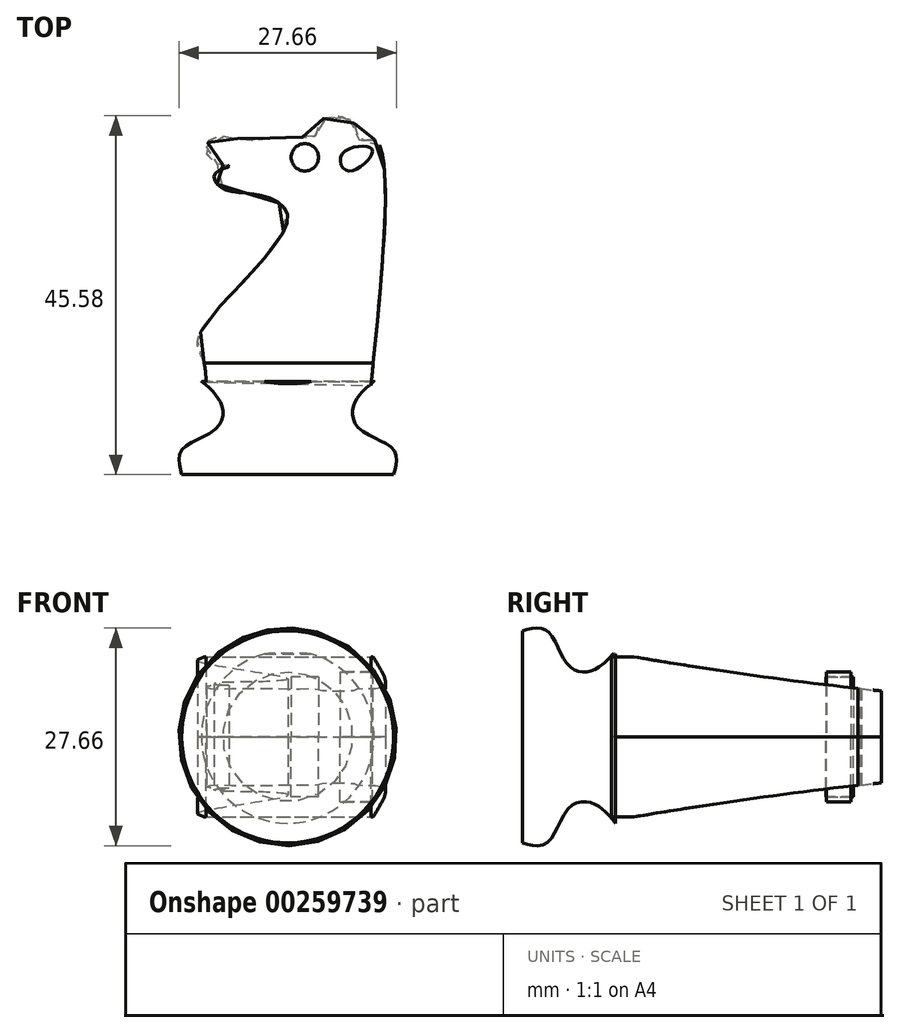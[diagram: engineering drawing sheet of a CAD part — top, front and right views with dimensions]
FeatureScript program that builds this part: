
annotation { "Feature Type Name" : "Feature", "Feature Type Description" : "" }
export const myFeature = defineFeature(function(context is Context, id is Id, definition is map)
    precondition{}
    {
        {
            var Q0;
            Q0=qCreatedBy(makeId("Top.planeOp"),FACE);
            var sketch = newSketch(context, id + "F0", { "sketchPlane" : qUnion([Q0])});
            skLineSegment(sketch, "E0", {"start": v(0, 0) * mm, "end": v(13.46, 0) * mm});
            skFitSpline(sketch, "E1", {"points": [v(13.46, 0) * mm, v(13.46, 3.13) * mm, v(9.08, 5.84) * mm, v(8.45, 8.97) * mm, v(10.97, 11.83) * mm], "startDerivative": vector(4.14, 14.83) * mm, "endDerivative": vector(11.05, 8.65) * mm});
            skLineSegment(sketch, "E2", {"start": v(0, 0) * mm, "end": v(0, 11.83) * mm});
            skLineSegment(sketch, "E3", {"start": v(0, 11.83) * mm, "end": v(10.97, 11.83) * mm});
            skSolve(sketch);
        }
        {
            var Q0;
            Q0=makeQuery(id+"F0.imprint","IMPRINT",FACE,{"disambiguationData":[TD([[makeQuery(id+"F0.imprint","IMPRINT",EDGE,{"derivedFrom":sQuery(id+"F0.wireOp",EDGE,"E0")}),1.0]])]});
            var Q1;
            Q1=sQuery(id+"F0.wireOp",EDGE,"E2");
            revolve(context, id + "F1", {"entities" : qUnion([Q0]), "axis" : qUnion([Q1]), "revolveType" : RevolveType.FULL});
        }
        {
            var Q0;
            Q0=qCreatedBy(makeId("Top.planeOp"),FACE);
            var sketch = newSketch(context, id + "F2", { "sketchPlane" : qUnion([Q0])});
            skFitSpline(sketch, "E4", {"points": [v(-10.37, 11.73) * mm, v(-10.79, 14.67) * mm, v(-11.2, 17.8) * mm, v(0, 32.26) * mm, v(-3.25, 35.4) * mm, v(-7.44, 36.04) * mm, v(-9.11, 37.08) * mm, v(-9.11, 38.34) * mm, v(-7.44, 39.18) * mm, v(-9.74, 39.8) * mm, v(-9.74, 42.74) * mm, v(-5.55, 42.53) * mm, v(0, 42.95) * mm, v(3.67, 43.16) * mm, v(4.3, 45.04) * mm, v(8.28, 44.83) * mm, v(9.11, 42.53) * mm, v(11, 42.53) * mm, v(10.58, 11.31) * mm], "startDerivative": vector(-2.35, 66.57) * mm, "endDerivative": vector(-30.17, -301.15) * mm});
            skLineSegment(sketch, "E5", {"start": v(-10.37, 11.73) * mm, "end": v(10.58, 11.31) * mm});
            skSolve(sketch);
        }
        {
            var Q0;
            Q0 = qSketchRegion(id + "F2", true);
            extrude(context, id + "F3", {"entities" : qUnion([Q0]), "depth" : 10.16 * mm});
        }
        {
            var Q0;
            Q0=makeQuery(id+"F2.imprint","IMPRINT",FACE,{"disambiguationData":[TD([[makeQuery(id+"F2.imprint","IMPRINT",EDGE,{"derivedFrom":sQuery(id+"F2.wireOp",EDGE,"E4")}),-1.0]])]});
            var sketch = newSketch(context, id + "F4", { "sketchPlane" : qUnion([Q0])});
            skCircle(sketch, "E6", {"center": v(2.17, 40.3) * mm, "radius": 1.73 * mm});
            skSolve(sketch);
        }
        {
            var Q0;
            Q0=makeQuery(id+"F2.imprint","IMPRINT",FACE,{"disambiguationData":[TD([[makeQuery(id+"F2.imprint","IMPRINT",EDGE,{"derivedFrom":sQuery(id+"F2.wireOp",EDGE,"E4")}),-1.0]])]});
            var sketch = newSketch(context, id + "F5", { "sketchPlane" : qUnion([Q0])});
            skFitSpline(sketch, "E7", {"points": [v(6.9, 40.71) * mm, v(10.46, 41.55) * mm, v(10.46, 40.3) * mm, v(7.53, 38.62) * mm, v(6.9, 40.71) * mm]});
            skSolve(sketch);
        }
        {
            var Q0;
            Q0=qCreatedBy(makeId("Right.planeOp"),FACE);
            var sketch = newSketch(context, id + "F6", { "sketchPlane" : qUnion([Q0])});
            skFitSpline(sketch, "E8", {"points": [v(76.54, 4.77) * mm, v(51.13, 5.34) * mm, v(7.54, 11.33) * mm], "startDerivative": vector(-52.97, -0.72) * mm, "endDerivative": vector(-64.6, 11.97) * mm});
            skLineSegment(sketch, "E9", {"start": v(76.54, 4.77) * mm, "end": v(76.54, 37.7) * mm});
            skLineSegment(sketch, "E10", {"start": v(76.54, 37.7) * mm, "end": v(7.54, 11.33) * mm});
            skSolve(sketch);
        }
        {
            var Q0;
            Q0=makeQuery(id+"F6.imprint","IMPRINT",FACE,{"disambiguationData":[TD([[makeQuery(id+"F6.imprint","IMPRINT",EDGE,{"derivedFrom":sQuery(id+"F6.wireOp",EDGE,"E8")}),-1.0]])]});
            extrude(context, id + "F7", {"entities" : qUnion([Q0]), "operationType" : NewBodyOperationType.REMOVE, "oppositeDirection" : true, "depth" : 25.4 * mm});
        }
        {
            var Q0;
            Q0 = qSketchRegion(id + "F6", true);
            extrude(context, id + "F8", {"entities" : qUnion([Q0]), "operationType" : NewBodyOperationType.REMOVE, "depth" : 25.4 * mm});
        }
        {
            var Q0;
            Q0 = qSketchRegion(id + "F4", true);
            extrude(context, id + "F9", {"entities" : qUnion([Q0]), "depth" : 7.62 * mm});
        }
        {
            var Q0;
            Q0 = qSketchRegion(id + "F5", true);
            extrude(context, id + "F10", {"entities" : qUnion([Q0]), "depth" : 8.25 * mm});
        }
        {
            var Q0;
            Q0=makeQuery(id+"F3.opExtrude","SWEPT_BODY",BODY,{"disambiguationData":[OSD([sQuery(id+"F2.wireOp",EDGE,"E4"),sQuery(id+"F2.wireOp",EDGE,"E5")])]});
            var Q1;
            Q1=makeQuery(id+"F10.opExtrude","SWEPT_BODY",BODY,{"disambiguationData":[OSD([sQuery(id+"F5.wireOp",EDGE,"E7")])]});
            var Q2;
            Q2=makeQuery(id+"F9.opExtrude","SWEPT_BODY",BODY,{"disambiguationData":[OSD([sQuery(id+"F4.wireOp",EDGE,"E6")])]});
            var Q3;
            Q3=qCreatedBy(makeId("Top.planeOp"),FACE);
            mirror(context, id + "F11", {"entities" : qUnion([Q0, Q1, Q2]), "mirrorPlane" : qUnion([Q3])});
        }
    });
